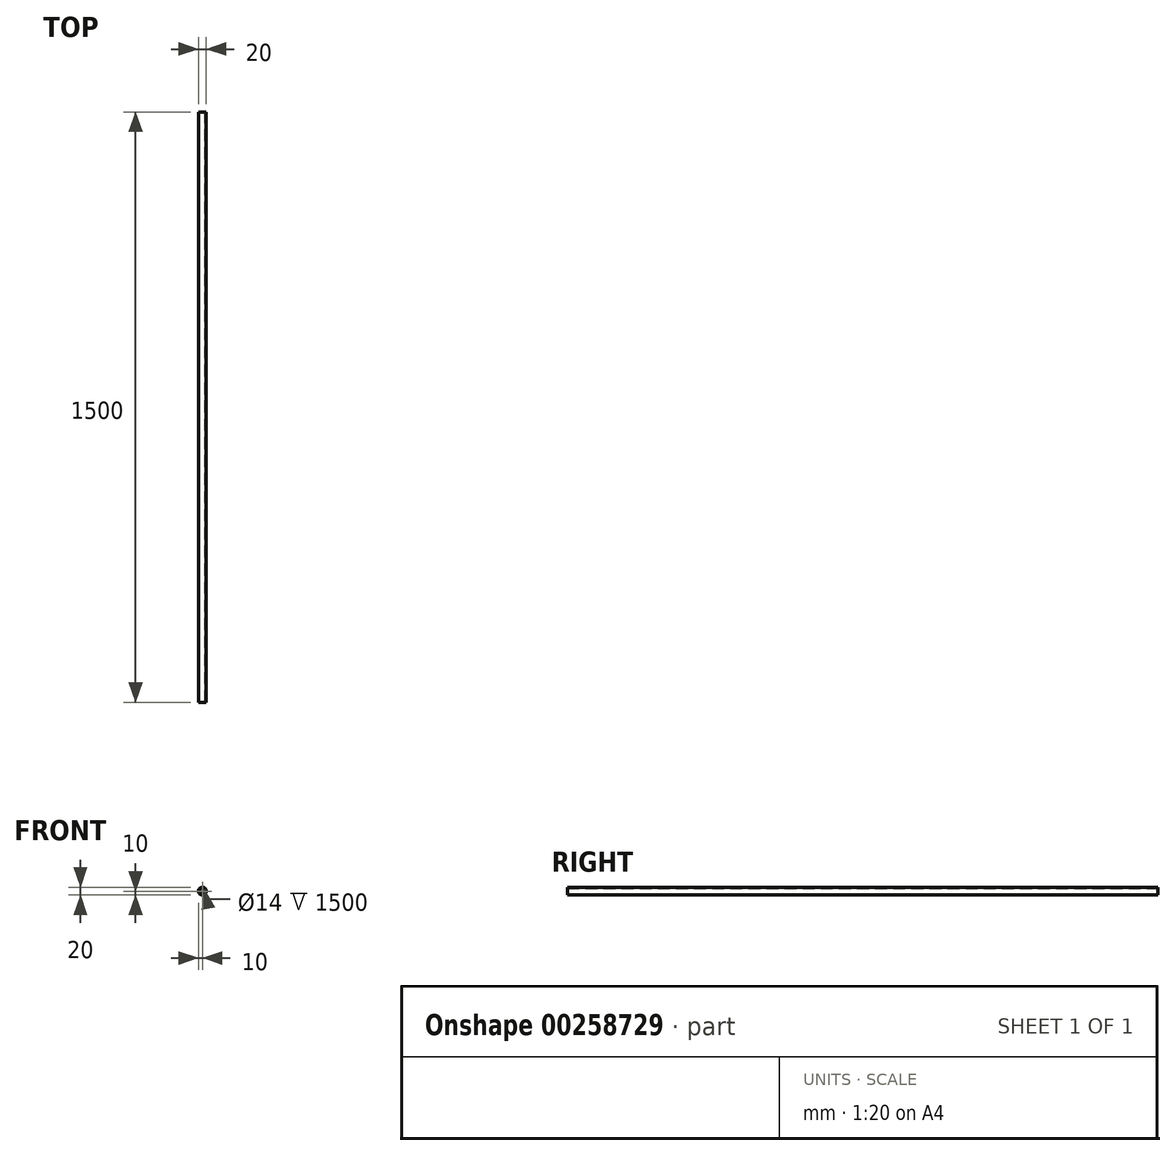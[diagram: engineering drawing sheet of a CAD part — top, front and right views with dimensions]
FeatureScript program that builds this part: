
annotation { "Feature Type Name" : "Feature", "Feature Type Description" : "" }
export const myFeature = defineFeature(function(context is Context, id is Id, definition is map)
    precondition{}
    {
        {
            var Q0;
            Q0=qCreatedBy(makeId("Front.planeOp"),FACE);
            var sketch = newSketch(context, id + "F0", { "sketchPlane" : qUnion([Q0])});
            skCircle(sketch, "E0", {"center": v(0, 0) * mm, "radius": 10 * mm});
            skCircle(sketch, "E1", {"center": v(0, 0) * mm, "radius": 7 * mm});
            skSolve(sketch);
        }
        {
            var Q0;
            Q0=makeQuery(id+"F0.imprint","IMPRINT",FACE,{"disambiguationData":[TD([[makeQuery(id+"F0.imprint","IMPRINT",EDGE,{"derivedFrom":sQuery(id+"F0.wireOp",EDGE,"E0")}),1.0]])]});
            extrude(context, id + "F1", {"entities" : qUnion([Q0]), "depth" : 1500 * mm});
        }
    });
